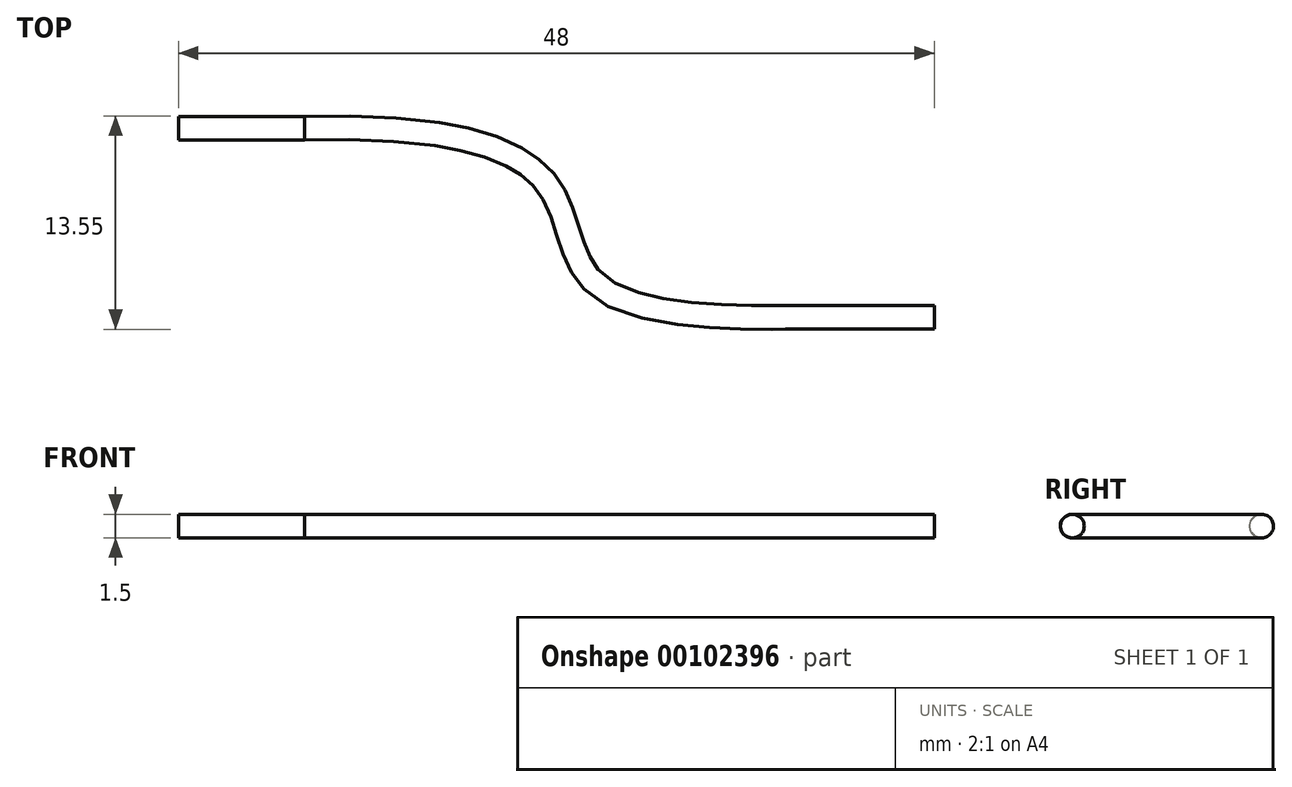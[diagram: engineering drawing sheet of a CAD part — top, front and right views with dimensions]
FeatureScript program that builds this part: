
annotation { "Feature Type Name" : "Feature", "Feature Type Description" : "" }
export const myFeature = defineFeature(function(context is Context, id is Id, definition is map)
    precondition{}
    {
        {
            var Q0;
            Q0=qCreatedBy(makeId("Top.planeOp"),FACE);
            var sketch = newSketch(context, id + "F0", { "sketchPlane" : qUnion([Q0])});
            skLineSegment(sketch, "E0", {"start": v(0, 0) * mm, "end": v(-8, 0) * mm});
            skLineSegment(sketch, "E1", {"start": v(-48, 12) * mm, "end": v(-40, 12) * mm});
            skFitSpline(sketch, "E2", {"points": [v(-40, 12) * mm, v(-24.23, 7.91) * mm, v(-20.93, 1.67) * mm, v(-8, 0) * mm], "startDerivative": vector(70.03, 1.78) * mm, "endDerivative": vector(19.1, 0) * mm});
            skSolve(sketch);
        }
        {
            var Q0;
            Q0=qCreatedBy(makeId("Right.planeOp"),FACE);
            var sketch = newSketch(context, id + "F1", { "sketchPlane" : qUnion([Q0])});
            skCircle(sketch, "E3", {"center": v(0, 0) * mm, "radius": 0.75 * mm});
            skSolve(sketch);
        }
        {
            var Q0;
            Q0=makeQuery(id+"F1.imprint","IMPRINT",FACE,{"disambiguationData":[TD([[makeQuery(id+"F1.imprint","IMPRINT",EDGE,{"derivedFrom":sQuery(id+"F1.wireOp",EDGE,"E3")}),1.0]])]});
            var Q1;
            Q1=sQuery(id+"F0.wireOp",EDGE,"E0");
            var Q2;
            Q2=sQuery(id+"F0.wireOp",EDGE,"E2");
            var Q3;
            Q3=sQuery(id+"F0.wireOp",EDGE,"E1");
            sweep(context, id + "F2", {"profiles" : qUnion([Q0]), "path" : qUnion([Q1, Q2, Q3])});
        }
    });
